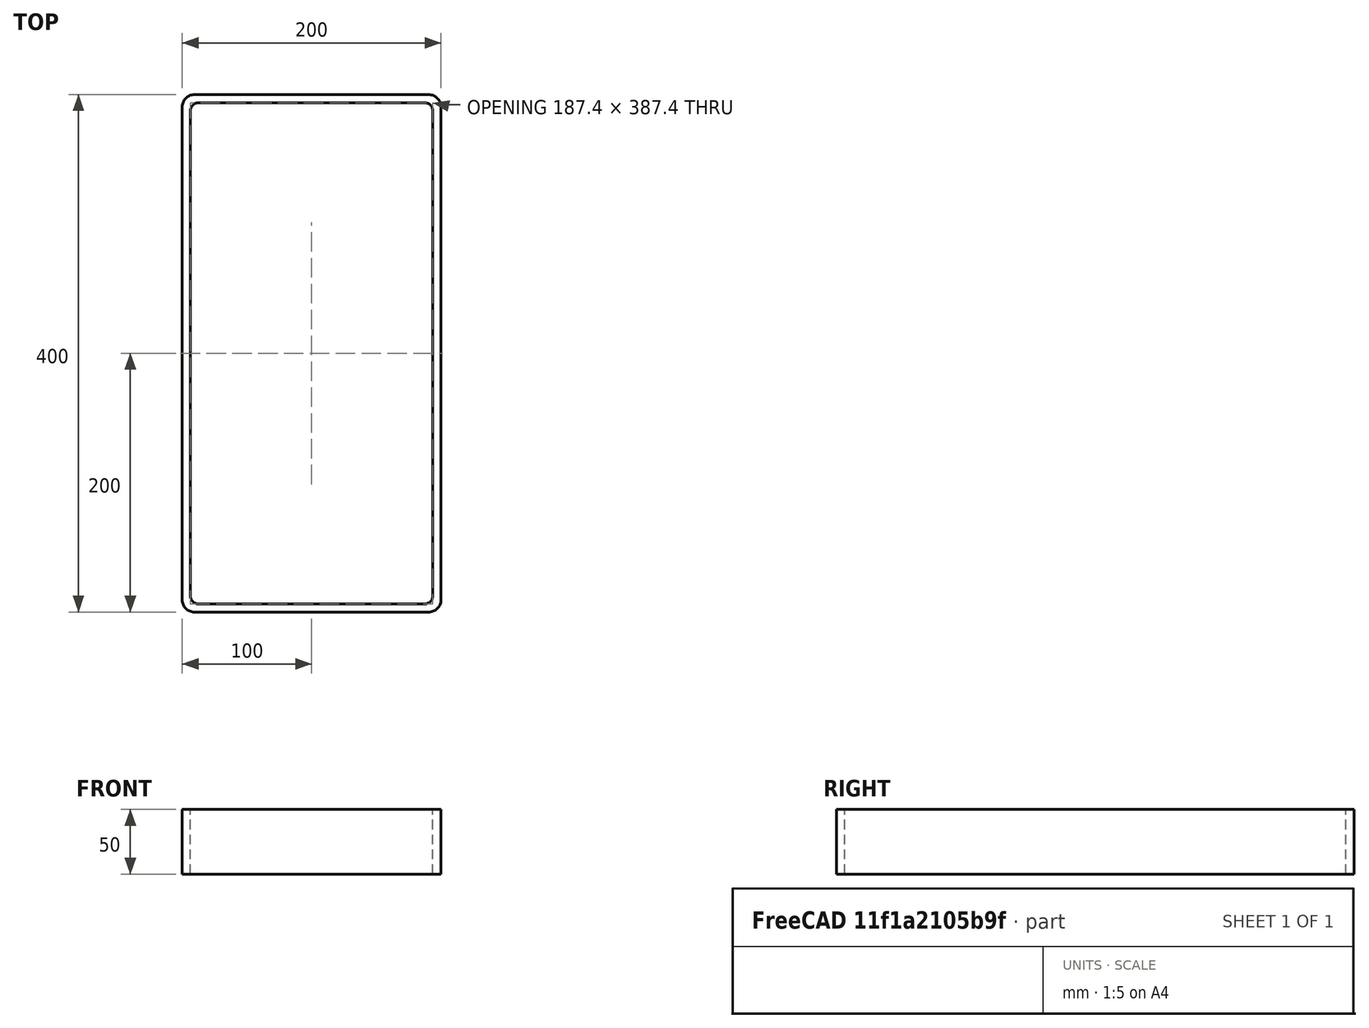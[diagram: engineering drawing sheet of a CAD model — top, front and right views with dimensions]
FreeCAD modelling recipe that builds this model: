
FCSTD DOCUMENT  (FreeCAD 0.15R4671 (Git))
Label: Rectangular hollow section 400x200x6.3 EN10219 S235JRH
License: All rights reserved
LicenseURL: http://en.wikipedia.org/wiki/All_rights_reserved
objects: Sketcher::SketchObject×1, Part::Extrusion×1
note: 2 computed .brp shape members not serialized (recipe doc carries the construction recipe); baked Part::Feature solids carry a one-line shape summary decoded from their .brp

FEATURE [Sketcher::SketchObject] Sketch
  sketch-geometry (16):
    g0: LineSegment StartX=-87.4 StartY=193.7 StartZ=0 EndX=87.4 EndY=193.7 EndZ=0
    g1: LineSegment StartX=93.7 StartY=187.4 StartZ=0 EndX=93.7 EndY=-187.4 EndZ=0
    g2: LineSegment StartX=87.4 StartY=-193.7 StartZ=0 EndX=-87.4 EndY=-193.7 EndZ=0
    g3: LineSegment StartX=-93.7 StartY=-187.4 StartZ=0 EndX=-93.7 EndY=187.4 EndZ=0
    g4: LineSegment StartX=-90.55 StartY=200 StartZ=0 EndX=90.55 EndY=200 EndZ=0
    g5: LineSegment StartX=100 StartY=190.55 StartZ=0 EndX=100 EndY=-190.55 EndZ=0
    g6: LineSegment StartX=90.55 StartY=-200 StartZ=0 EndX=-90.55 EndY=-200 EndZ=0
    g7: LineSegment StartX=-100 StartY=-190.55 StartZ=0 EndX=-100 EndY=190.55 EndZ=0
    g8: ArcOfCircle CenterX=-87.4 CenterY=187.4 CenterZ=0 NormalX=0 NormalY=0 NormalZ=1 Radius=6.3 StartAngle=1.5708 EndAngle=3.14159
    g9: ArcOfCircle CenterX=87.4 CenterY=187.4 CenterZ=0 NormalX=0 NormalY=0 NormalZ=1 Radius=6.3 StartAngle=0 EndAngle=1.5708
    g10: ArcOfCircle CenterX=87.4 CenterY=-187.4 CenterZ=0 NormalX=0 NormalY=0 NormalZ=1 Radius=6.3 StartAngle=4.71239 EndAngle=6.28319
    g11: ArcOfCircle CenterX=-87.4 CenterY=-187.4 CenterZ=0 NormalX=0 NormalY=0 NormalZ=1 Radius=6.3 StartAngle=3.14159 EndAngle=4.71239
    g12: ArcOfCircle CenterX=90.55 CenterY=190.55 CenterZ=0 NormalX=0 NormalY=0 NormalZ=1 Radius=9.45 StartAngle=0 EndAngle=1.5708
    g13: ArcOfCircle CenterX=90.55 CenterY=-190.55 CenterZ=0 NormalX=0 NormalY=0 NormalZ=1 Radius=9.45 StartAngle=4.71239 EndAngle=6.28319
    g14: ArcOfCircle CenterX=-90.55 CenterY=-190.55 CenterZ=0 NormalX=0 NormalY=0 NormalZ=1 Radius=9.45 StartAngle=3.14159 EndAngle=4.71239
    g15: ArcOfCircle CenterX=-90.55 CenterY=190.55 CenterZ=0 NormalX=0 NormalY=0 NormalZ=1 Radius=9.45 StartAngle=1.5708 EndAngle=3.14159
  constraints (36):
    c: Horizontal(g2)
    c: Vertical(g3)
    c: Horizontal(g6)
    c: Vertical(g7)
    c: Tangent(g3,g8) = 1.5708
    c: Tangent(g0,g8) = 1.5708
    c: Tangent(g0,g9) = 1.5708
    c: Tangent(g1,g9) = 1.5708
    c: Tangent(g1,g10) = 1.5708
    c: Tangent(g2,g10) = 1.5708
    c: Tangent(g2,g11) = 1.5708
    c: Tangent(g3,g11) = 1.5708
    c: Tangent(g4,g12) = 1.5708
    c: Tangent(g5,g12) = 1.5708
    c: Tangent(g5,g13) = 1.5708
    c: Tangent(g6,g13) = 1.5708
    c: Tangent(g6,g14) = 1.5708
    c: Tangent(g7,g14) = 1.5708
    c: Tangent(g7,g15) = 1.5708
    c: Tangent(g4,g15) = 1.5708
    c: Equal(g9,g8)
    c: Equal(g9,g11)
    c: Equal(g9,g10)
    c: Equal(g12,g15)
    c: Equal(g12,g14)
    c: Equal(g12,g13)
    c: Symmetric(g4,g6,g-1)
    c: Symmetric(g7,g5,g-2)
    c: DistanceY(g4,g6) = -400
    c: DistanceX(g7,g5) = 200
    c: Symmetric(g3,g1,g-2)
    c: Symmetric(g0,g2,g-1)
    c: DistanceY(g0,g4) = 6.3
    c: DistanceX(g5,g1) = -6.3
    c: Radius(g9) = 6.3
    c: Radius(g12) = 9.45
FEATURE [Part::Extrusion] Extrude  label="Rectangular hollow section 400x200x6.3 EN10219 S235JRH"
  Base = -> Sketch
  Dir = (0,0,50)
  Solid = true
